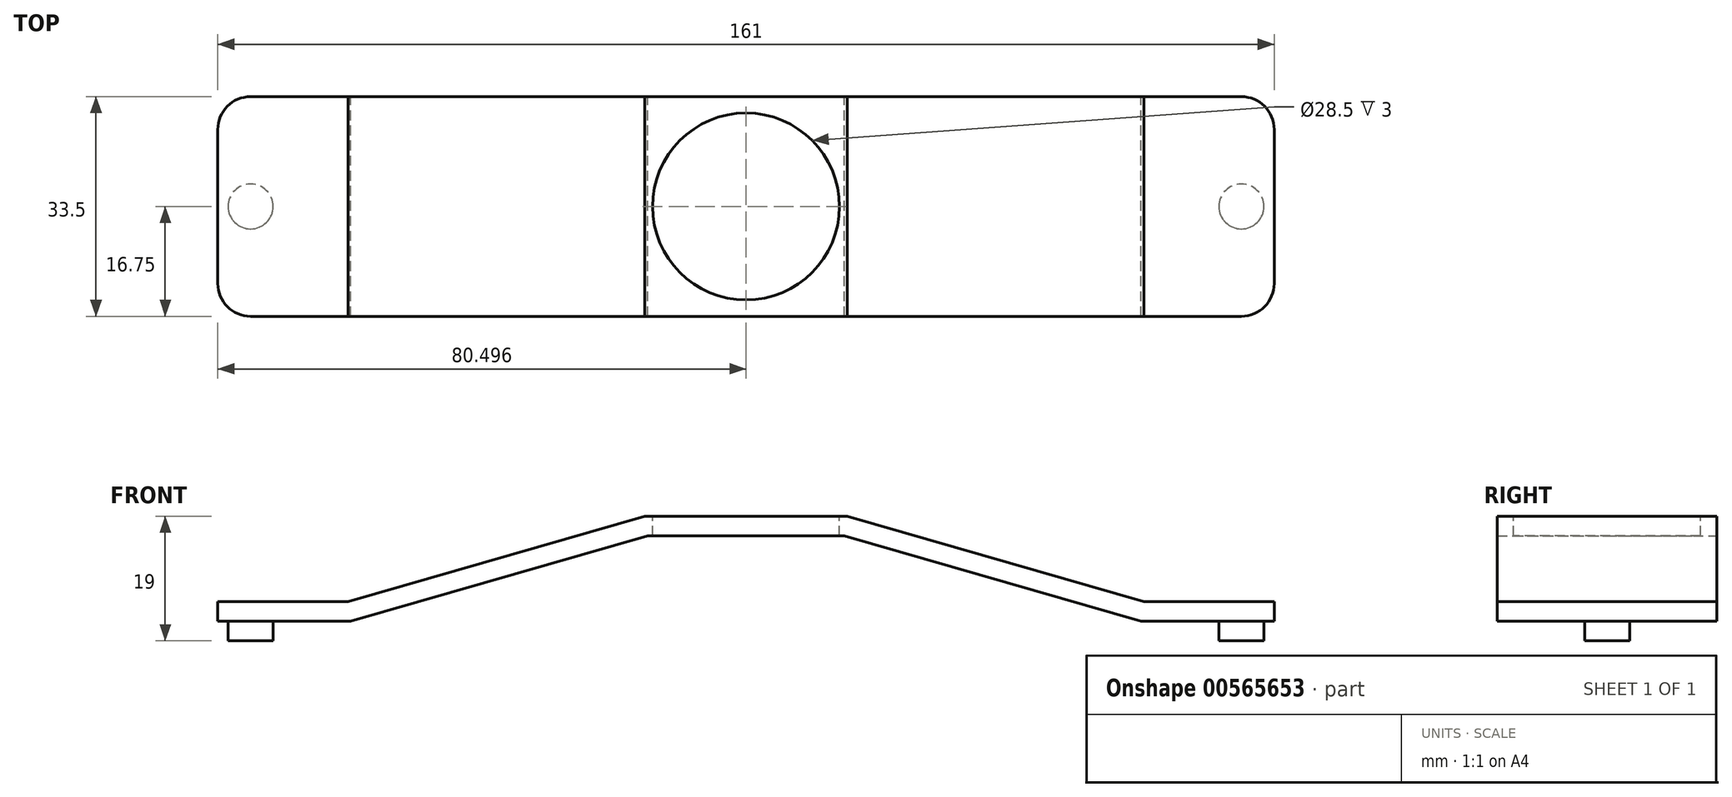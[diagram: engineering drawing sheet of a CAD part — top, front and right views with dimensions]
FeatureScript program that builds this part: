
annotation { "Feature Type Name" : "Feature", "Feature Type Description" : "" }
export const myFeature = defineFeature(function(context is Context, id is Id, definition is map)
    precondition{}
    {
        {
            assignVariable(context, id + "F0", {"name" : "wd", "anyValue" : 28.5});
        }
        {
            var Q0;
            Q0=qCreatedBy(makeId("Front.planeOp"),FACE);
            var sketch = newSketch(context, id + "F1", { "sketchPlane" : qUnion([Q0])});
            skPoint(sketch, "E0.middle", {"position": v(0, 0) * mm});
            skLineSegment(sketch, "E1", {"start": v(-57.97, -10.12) * mm, "end": v(57.03, -10.12) * mm, "construction": true});
            skLineSegment(sketch, "E2", {"start": v(-84.06, 0) * mm, "end": v(-63.8, 0) * mm});
            skLineSegment(sketch, "E3", {"start": v(-18.56, 13) * mm, "end": v(11.44, 13) * mm});
            skLineSegment(sketch, "E4", {"start": v(11.44, 13) * mm, "end": v(56.67, 0) * mm});
            skLineSegment(sketch, "E5", {"start": v(56.67, 0) * mm, "end": v(76.94, 0) * mm});
            skLineSegment(sketch, "E6", {"start": v(-18.56, 13) * mm, "end": v(-63.8, 0) * mm});
            skLineSegment(sketch, "E7.0", {"start": v(57.1, 3) * mm, "end": v(76.94, 3) * mm});
            skLineSegment(sketch, "E7.1", {"start": v(-84.06, 3) * mm, "end": v(-64.22, 3) * mm});
            skLineSegment(sketch, "E7.2", {"start": v(-18.99, 16) * mm, "end": v(-64.22, 3) * mm});
            skLineSegment(sketch, "E7.3", {"start": v(-18.99, 16) * mm, "end": v(11.86, 16) * mm});
            skLineSegment(sketch, "E7.4", {"start": v(11.86, 16) * mm, "end": v(57.1, 3) * mm});
            skLineSegment(sketch, "E8", {"start": v(-84.06, 3) * mm, "end": v(-84.06, 0) * mm});
            skLineSegment(sketch, "E9", {"start": v(76.94, 3) * mm, "end": v(76.94, 0) * mm});
            skPoint(sketch, "E10", {"position": v(-3.56, 16) * mm});
            skPoint(sketch, "E11", {"position": v(-79.06, 0) * mm});
            skPoint(sketch, "E12", {"position": v(71.94, 0) * mm});
            skLineSegment(sketch, "E13", {"start": v(-84.06, 0) * mm, "end": v(76.94, 0) * mm, "construction": true});
            skLineSegment(sketch, "E14", {"start": v(56.67, 0) * mm, "end": v(71.94, 0) * mm, "construction": true});
            skLineSegment(sketch, "E15", {"start": v(-63.8, 0) * mm, "end": v(-79.06, 0) * mm, "construction": true});
            skLineSegment(sketch, "E16", {"start": v(-41.18, 6.5) * mm, "end": v(-42, 9.38) * mm, "construction": true});
            skLineSegment(sketch, "E17", {"start": v(34.05, 6.5) * mm, "end": v(34.88, 9.38) * mm, "construction": true});
            skLineSegment(sketch, "E18", {"start": v(-3.56, 13) * mm, "end": v(-3.56, 16) * mm, "construction": true});
            skLineSegment(sketch, "E19", {"start": v(-41.18, 6.5) * mm, "end": v(-41.18, 0) * mm, "construction": true});
            skSolve(sketch);
        }
        {
            var Q0;
            Q0=makeQuery(id+"F1.imprint","IMPRINT",FACE,{"disambiguationData":[TD([[makeQuery(id+"F1.imprint","IMPRINT",EDGE,{"derivedFrom":sQuery(id+"F1.wireOp",EDGE,"E2")}),1.0]])]});
            extrude(context, id + "F2", {"entities" : qUnion([Q0]), "endBound" : BoundingType.SYMMETRIC, "depth" : ((getVariable(context, 'wd')) + 5) * mm, "offsetDistance" : 25 * mm});
        }
        {
            var Q0;
            Q0=makeQuery(id+"F2.opExtrude","SWEPT_FACE",FACE,{"disambiguationData":[OSD([sQuery(id+"F1.wireOp",EDGE,"E7.3")])]});
            var sketch = newSketch(context, id + "F3", { "sketchPlane" : qUnion([Q0])});
            skCircle(sketch, "E20", {"center": v(-3.56, 0) * mm, "radius": 14.25 * mm});
            skLineSegment(sketch, "E21", {"start": v(-3.56, 16.75) * mm, "end": v(-3.56, -16.75) * mm, "construction": true});
            skLineSegment(sketch, "E22", {"start": v(-18.99, 0) * mm, "end": v(11.86, 0) * mm, "construction": true});
            skLineSegment(sketch, "E23.bottom", {"start": v(-18.96, 14.25) * mm, "end": v(11.83, 14.25) * mm});
            skLineSegment(sketch, "E23.top", {"start": v(-18.96, -14.25) * mm, "end": v(11.83, -14.25) * mm});
            skLineSegment(sketch, "E23.left", {"start": v(-18.96, 14.25) * mm, "end": v(-18.96, -14.25) * mm});
            skLineSegment(sketch, "E23.right", {"start": v(11.83, 14.25) * mm, "end": v(11.83, -14.25) * mm});
            skSolve(sketch);
        }
        {
            var Q0;
            {var subQ0=sQuery(id+"F3.wireOp",EDGE,"E20");var subQ1=sQuery(id+"F1.wireOp",EDGE,"E7.3");var subQ2=makeQuery(id+"F3.imprint","INTERSECT",VERTEX,{"derivedFrom":[makeQuery(id+"F2.opExtrude","CAP_EDGE",EDGE,{"disambiguationData":[OSD([subQ1])],"isStart":true}),subQ0]});Q0=makeQuery(id+"F3.imprint","IMPRINT",FACE,{"disambiguationData":[TD([[makeQuery(id+"F3.imprint","IMPRINT",EDGE,{"disambiguationData":[TD([[subQ2,-1.0]])],"derivedFrom":subQ0}),1.0]])]});}
            extrude(context, id + "F4", {"entities" : qUnion([Q0]), "operationType" : NewBodyOperationType.REMOVE, "endBound" : BoundingType.THROUGH_ALL, "oppositeDirection" : true, "depth" : 25 * mm, "offsetDistance" : 25 * mm});
        }
        {
            var Q0;
            Q0=makeQuery(id+"F2.opExtrude","SWEPT_FACE",FACE,{"disambiguationData":[OSD([sQuery(id+"F1.wireOp",EDGE,"E2")])]});
            var sketch = newSketch(context, id + "F5", { "sketchPlane" : qUnion([Q0])});
            skCircle(sketch, "E24", {"center": v(-79.06, 0) * mm, "radius": 3.43 * mm});
            skLineSegment(sketch, "E25", {"start": v(-63.8, 0) * mm, "end": v(-84.06, 0) * mm, "construction": true});
            skLineSegment(sketch, "E26", {"start": v(-84.06, 0) * mm, "end": v(57.49, 0) * mm, "construction": true});
            skSolve(sketch);
        }
        {
            var Q0;
            Q0=makeQuery(id+"F2.opExtrude","SWEPT_FACE",FACE,{"disambiguationData":[OSD([sQuery(id+"F1.wireOp",EDGE,"E5")])]});
            var sketch = newSketch(context, id + "F6", { "sketchPlane" : qUnion([Q0])});
            skPoint(sketch, "E27", {"position": v(71.94, 0) * mm});
            skCircle(sketch, "E28", {"center": v(71.94, 0) * mm, "radius": 3.43 * mm});
            skSolve(sketch);
        }
        {
            var Q0;
            Q0=makeQuery(id+"F5.imprint","IMPRINT",FACE,{"disambiguationData":[TD([[makeQuery(id+"F5.imprint","IMPRINT",EDGE,{"derivedFrom":sQuery(id+"F5.wireOp",EDGE,"E24")}),1.0]])]});
            var Q1;
            Q1=makeQuery(id+"F6.imprint","IMPRINT",FACE,{"disambiguationData":[TD([[makeQuery(id+"F6.imprint","IMPRINT",EDGE,{"derivedFrom":sQuery(id+"F6.wireOp",EDGE,"E28")}),1.0]])]});
            extrude(context, id + "F7", {"entities" : qUnion([Q0, Q1]), "operationType" : NewBodyOperationType.ADD, "depth" : 6 / 2 * mm, "offsetDistance" : 25 * mm});
        }
        {
            var Q0;
            Q0=makeQuery(id+"F2.opExtrude","CAP_EDGE",EDGE,{"disambiguationData":[OSD([sQuery(id+"F1.wireOp",EDGE,"E8")])],"isStart":false});
            fillet(context, id + "F8", {"entities" : qUnion([Q0]), "radius" : 5 * mm, "tangentPropagation" : true, "allowEdgeOverflow" : false});
        }
        {
            var Q0;
            Q0=makeQuery(id+"F2.opExtrude","CAP_EDGE",EDGE,{"disambiguationData":[OSD([sQuery(id+"F1.wireOp",EDGE,"E8")])],"isStart":true});
            fillet(context, id + "F9", {"entities" : qUnion([Q0]), "radius" : 5 * mm, "tangentPropagation" : true, "allowEdgeOverflow" : false});
        }
        {
            var Q0;
            Q0=makeQuery(id+"F2.opExtrude","CAP_EDGE",EDGE,{"disambiguationData":[OSD([sQuery(id+"F1.wireOp",EDGE,"E9")])],"isStart":false});
            fillet(context, id + "F10", {"entities" : qUnion([Q0]), "radius" : 5 * mm, "tangentPropagation" : true, "allowEdgeOverflow" : false});
        }
        {
            var Q0;
            Q0=makeQuery(id+"F2.opExtrude","CAP_EDGE",EDGE,{"disambiguationData":[OSD([sQuery(id+"F1.wireOp",EDGE,"E9")])],"isStart":true});
            fillet(context, id + "F11", {"entities" : qUnion([Q0]), "radius" : 5 * mm, "tangentPropagation" : true, "allowEdgeOverflow" : false});
        }
    });
